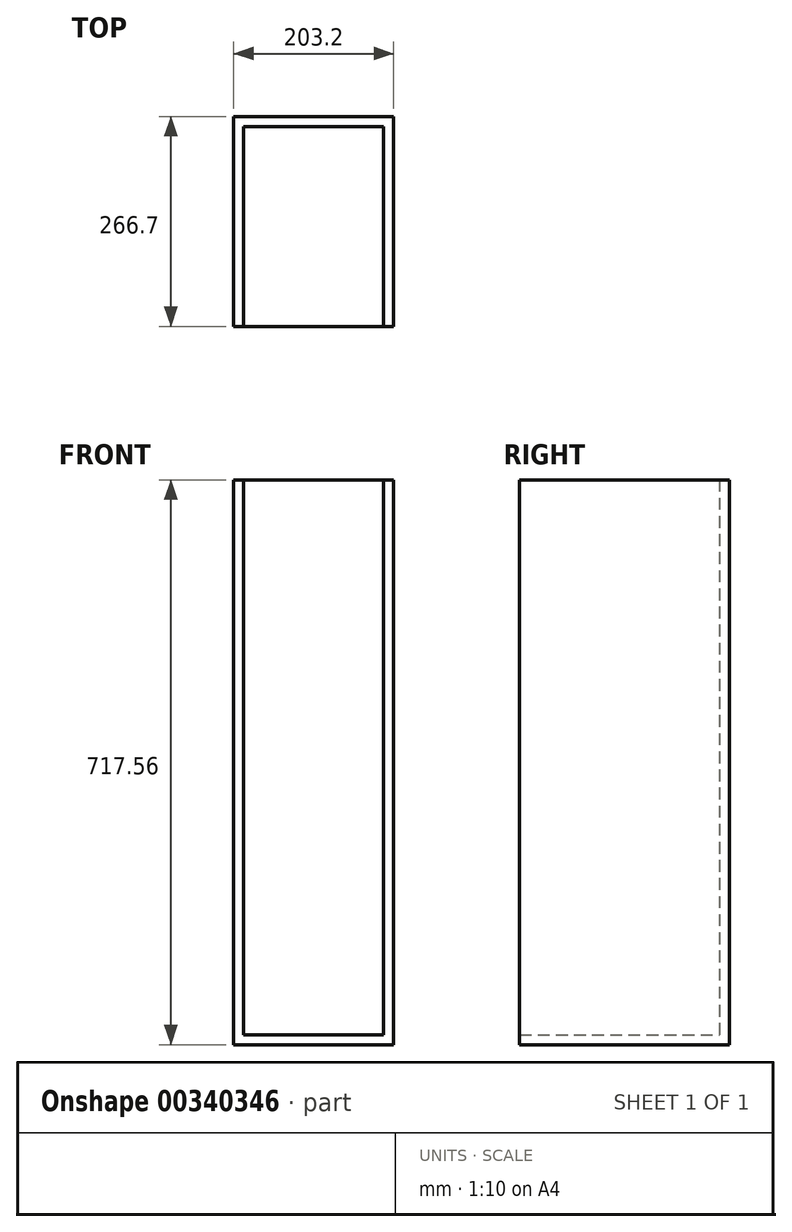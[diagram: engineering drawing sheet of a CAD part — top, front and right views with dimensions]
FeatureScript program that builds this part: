
annotation { "Feature Type Name" : "Feature", "Feature Type Description" : "" }
export const myFeature = defineFeature(function(context is Context, id is Id, definition is map)
    precondition{}
    {
        {
            var Q0;
            Q0=qCreatedBy(makeId("Front.planeOp"),FACE);
            var sketch = newSketch(context, id + "F0", { "sketchPlane" : qUnion([Q0])});
            skLineSegment(sketch, "E0.bottom", {"start": v(101.6, -358.78) * mm, "end": v(-101.6, -358.78) * mm});
            skLineSegment(sketch, "E0.top", {"start": v(101.6, 358.77) * mm, "end": v(-101.6, 358.77) * mm});
            skLineSegment(sketch, "E0.left", {"start": v(101.6, -358.78) * mm, "end": v(101.6, 358.77) * mm});
            skLineSegment(sketch, "E0.right", {"start": v(-101.6, -358.78) * mm, "end": v(-101.6, 358.77) * mm});
            skPoint(sketch, "E0.middle", {"position": v(0, 0) * mm});
            skSolve(sketch);
        }
        {
            var Q0;
            Q0=makeQuery(id+"F0.imprint","IMPRINT",FACE,{"disambiguationData":[TD([[makeQuery(id+"F0.imprint","IMPRINT",EDGE,{"derivedFrom":sQuery(id+"F0.wireOp",EDGE,"E0.bottom")}),-1.0]])]});
            extrude(context, id + "F1", {"entities" : qUnion([Q0]), "depth" : 12.7 * mm});
        }
        {
            var Q0;
            Q0=makeQuery(id+"F1.opExtrude","CAP_FACE",FACE,{"disambiguationData":[OSD([sQuery(id+"F0.wireOp",EDGE,"E0.bottom"),sQuery(id+"F0.wireOp",EDGE,"E0.top"),sQuery(id+"F0.wireOp",EDGE,"E0.left"),sQuery(id+"F0.wireOp",EDGE,"E0.right")])],"isStart":false});
            var sketch = newSketch(context, id + "F2", { "sketchPlane" : qUnion([Q0])});
            skLineSegment(sketch, "E1.bottom", {"start": v(-101.6, -358.78) * mm, "end": v(101.6, -358.78) * mm});
            skLineSegment(sketch, "E1.top", {"start": v(-101.6, -346.08) * mm, "end": v(101.6, -346.08) * mm});
            skLineSegment(sketch, "E1.left", {"start": v(-101.6, -358.78) * mm, "end": v(-101.6, -346.08) * mm});
            skLineSegment(sketch, "E1.right", {"start": v(101.6, -358.78) * mm, "end": v(101.6, -346.08) * mm});
            skSolve(sketch);
        }
        {
            var Q0;
            Q0=makeQuery(id+"F2.imprint","IMPRINT",FACE,{"disambiguationData":[TD([[makeQuery(id+"F2.imprint","IMPRINT",EDGE,{"derivedFrom":sQuery(id+"F2.wireOp",EDGE,"E1.bottom")}),-1.0]])]});
            extrude(context, id + "F3", {"entities" : qUnion([Q0]), "operationType" : NewBodyOperationType.ADD, "depth" : 254 * mm});
        }
        {
            var Q0;
            Q0=makeQuery(id+"F1.opExtrude","CAP_FACE",FACE,{"disambiguationData":[OSD([sQuery(id+"F0.wireOp",EDGE,"E0.bottom"),sQuery(id+"F0.wireOp",EDGE,"E0.top"),sQuery(id+"F0.wireOp",EDGE,"E0.left"),sQuery(id+"F0.wireOp",EDGE,"E0.right")])],"isStart":false});
            var sketch = newSketch(context, id + "F4", { "sketchPlane" : qUnion([Q0])});
            skLineSegment(sketch, "E2.bottom", {"start": v(-101.6, 358.77) * mm, "end": v(-88.9, 358.77) * mm});
            skLineSegment(sketch, "E2.top", {"start": v(-101.6, -346.08) * mm, "end": v(-88.9, -346.08) * mm});
            skLineSegment(sketch, "E2.left", {"start": v(-101.6, 358.77) * mm, "end": v(-101.6, -346.08) * mm});
            skLineSegment(sketch, "E2.right", {"start": v(-88.9, 358.77) * mm, "end": v(-88.9, -346.08) * mm});
            skLineSegment(sketch, "E3.bottom", {"start": v(101.6, 358.77) * mm, "end": v(88.9, 358.77) * mm});
            skLineSegment(sketch, "E3.top", {"start": v(101.6, -346.08) * mm, "end": v(88.9, -346.08) * mm});
            skLineSegment(sketch, "E3.left", {"start": v(101.6, 358.77) * mm, "end": v(101.6, -346.08) * mm});
            skLineSegment(sketch, "E3.right", {"start": v(88.9, 358.77) * mm, "end": v(88.9, -346.08) * mm});
            skSolve(sketch);
        }
        {
            var Q0;
            Q0=makeQuery(id+"F4.imprint","IMPRINT",FACE,{"disambiguationData":[TD([[makeQuery(id+"F4.imprint","IMPRINT",EDGE,{"derivedFrom":sQuery(id+"F4.wireOp",EDGE,"E2.bottom")}),1.0]])]});
            var Q1;
            Q1=makeQuery(id+"F4.imprint","IMPRINT",FACE,{"disambiguationData":[TD([[makeQuery(id+"F4.imprint","IMPRINT",EDGE,{"derivedFrom":sQuery(id+"F4.wireOp",EDGE,"E3.bottom")}),1.0]])]});
            extrude(context, id + "F5", {"entities" : qUnion([Q0, Q1]), "operationType" : NewBodyOperationType.ADD, "depth" : 254 * mm});
        }
    });
